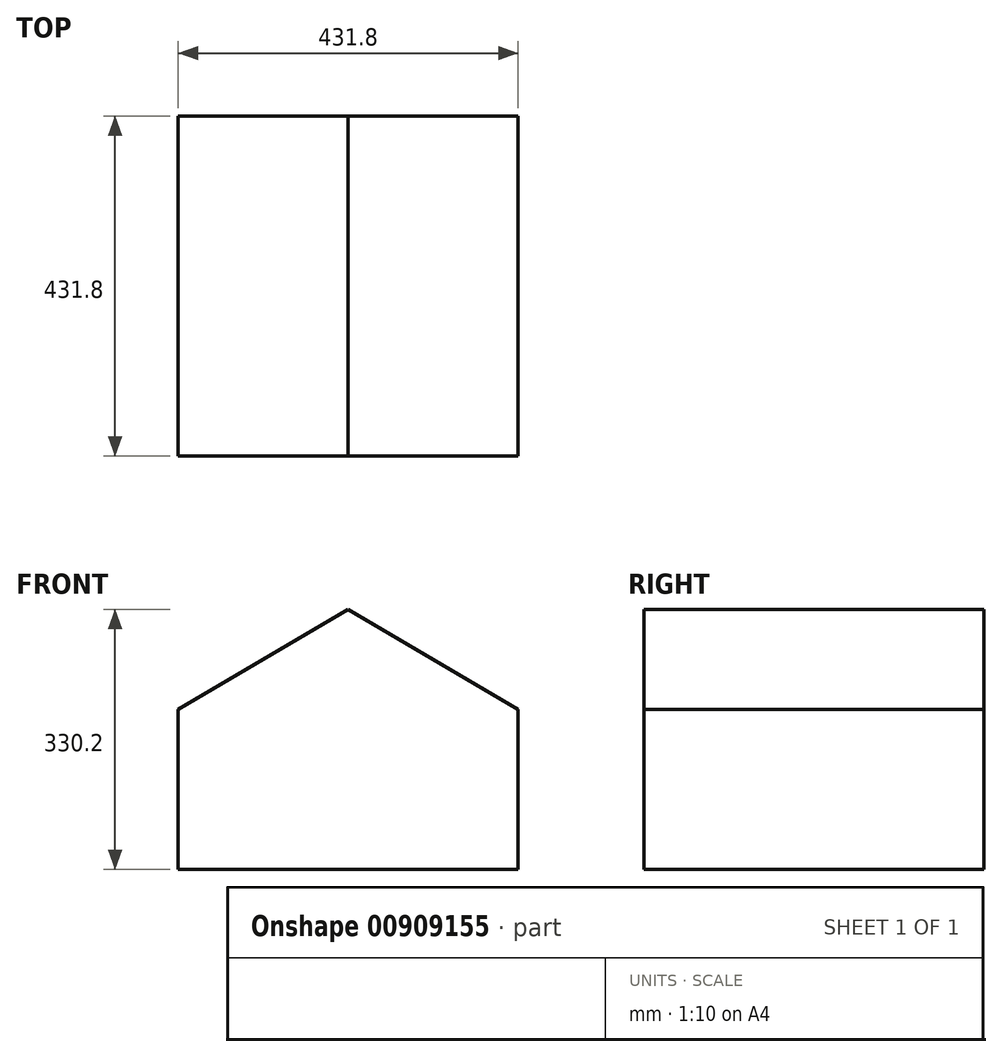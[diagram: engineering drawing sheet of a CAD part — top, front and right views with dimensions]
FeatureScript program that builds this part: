
annotation { "Feature Type Name" : "Feature", "Feature Type Description" : "" }
export const myFeature = defineFeature(function(context is Context, id is Id, definition is map)
    precondition{}
    {
        {
            var Q0;
            Q0=qCreatedBy(makeId("Front.planeOp"),FACE);
            var sketch = newSketch(context, id + "F0", { "sketchPlane" : qUnion([Q0])});
            skLineSegment(sketch, "E0.bottom", {"start": v(215.9, -101.6) * mm, "end": v(-215.9, -101.6) * mm});
            skLineSegment(sketch, "E0.left", {"start": v(215.9, -101.6) * mm, "end": v(215.9, 101.6) * mm});
            skLineSegment(sketch, "E0.right", {"start": v(-215.9, -101.6) * mm, "end": v(-215.9, 101.6) * mm});
            skPoint(sketch, "E0.middle", {"position": v(0, 0) * mm});
            skLineSegment(sketch, "E1", {"start": v(0, 228.6) * mm, "end": v(-215.9, 101.6) * mm});
            skLineSegment(sketch, "E2", {"start": v(0, 228.6) * mm, "end": v(215.9, 101.6) * mm});
            skPoint(sketch, "E3.start.orphan", {"position": v(0, 101.6) * mm});
            skSolve(sketch);
        }
        {
            var Q0;
            Q0=makeQuery(id+"F0.imprint","IMPRINT",FACE,{"disambiguationData":[TD([[makeQuery(id+"F0.imprint","IMPRINT",EDGE,{"derivedFrom":sQuery(id+"F0.wireOp",EDGE,"E0.bottom")}),-1.0]])]});
            extrude(context, id + "F1", {"entities" : qUnion([Q0]), "endBound" : BoundingType.SYMMETRIC, "depth" : 431.8 * mm, "offsetDistance" : 25.4 * mm});
        }
    });
